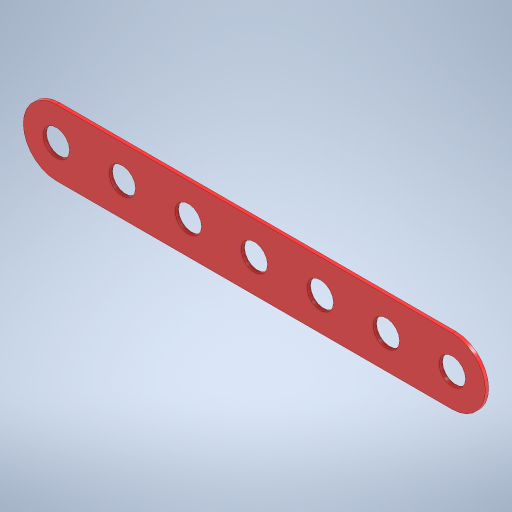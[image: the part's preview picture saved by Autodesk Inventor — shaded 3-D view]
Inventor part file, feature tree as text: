
AUTODESK INVENTOR PART (.ipt)
format: ipt  version: 2024 (Build 280153000, 153)  size: 257,536 bytes
history: native  units: mm
features: extrude x2, sketch x2, other x1, pattern_linear x1
ambient origin geometry x8: Origin, YZ Plane, XZ Plane, XY Plane, X Axis, Y Axis, Z Axis, Center Point
bodies: Body1 (feature_tree)
feature tree (6):
  other  "Těleso1"
  extrude  "Vysunutí1"  Depth=35.0mm
  extrude  "Vysunutí2"  Depth=5.0mm
  pattern_linear  "Obdélníkové pole1"  Spacing1=0.5mm  [1 undecoded]
  sketch  "Náčrt1"
  sketch  "Náčrt2"
note: 1 required parameter value undecoded (feature->parameter linkage not recoverable at this tier; creation-order binding heuristic only, values carry confidence <= 0.55)
